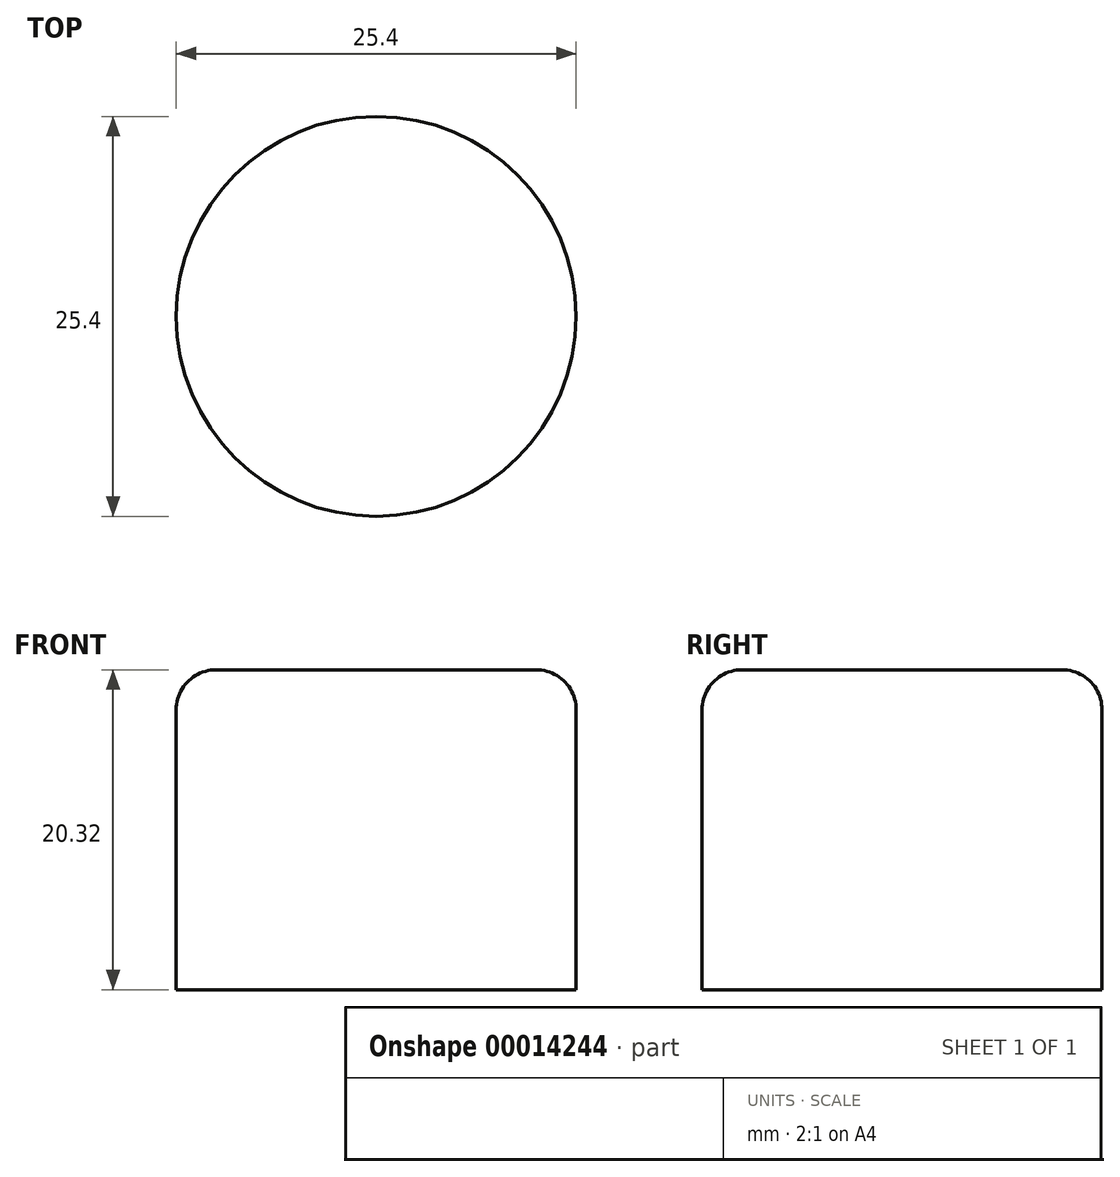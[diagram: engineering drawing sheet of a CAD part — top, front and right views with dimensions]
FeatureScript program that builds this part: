
annotation { "Feature Type Name" : "Feature", "Feature Type Description" : "" }
export const myFeature = defineFeature(function(context is Context, id is Id, definition is map)
    precondition{}
    {
        {
            var Q0;
            Q0=qCreatedBy(makeId("Top.planeOp"),FACE);
            var sketch = newSketch(context, id + "F0", { "sketchPlane" : qUnion([Q0])});
            skCircle(sketch, "E0", {"center": v(0, 0) * mm, "radius": 12.7 * mm});
            skSolve(sketch);
        }
        {
            var Q0;
            Q0=makeQuery(id+"F0.imprint","IMPRINT",FACE,{"disambiguationData":[TD([[makeQuery(id+"F0.imprint","IMPRINT",EDGE,{"derivedFrom":sQuery(id+"F0.wireOp",EDGE,"E0")}),1.0]])]});
            extrude(context, id + "F1", {"entities" : qUnion([Q0]), "depth" : 20.32 * mm});
        }
        {
            var Q0;
            Q0=makeQuery(id+"F1.opExtrude","CAP_EDGE",EDGE,{"disambiguationData":[OSD([sQuery(id+"F0.wireOp",EDGE,"E0")])],"isStart":false});
            fillet(context, id + "F2", {"entities" : qUnion([Q0]), "radius" : 2.54 * mm, "tangentPropagation" : true, "allowEdgeOverflow" : false});
        }
    });
